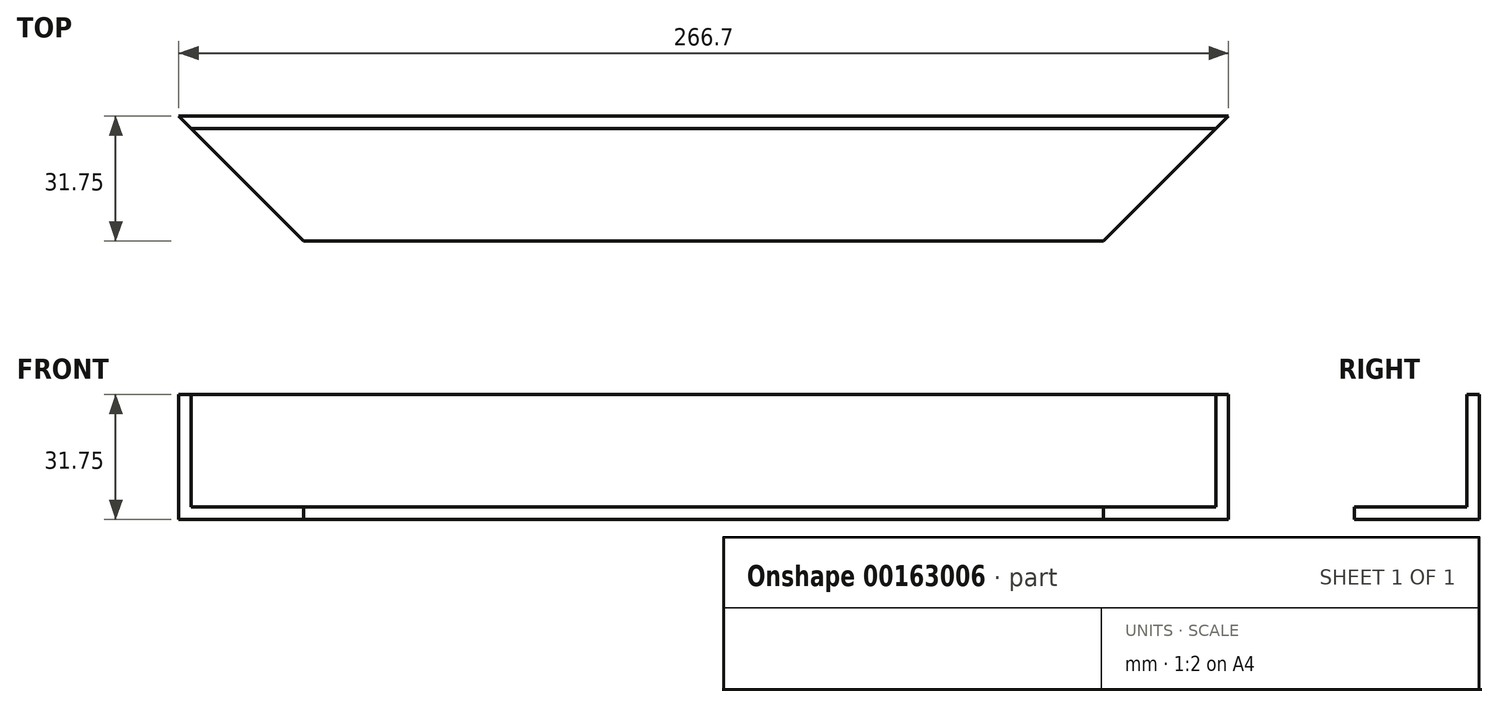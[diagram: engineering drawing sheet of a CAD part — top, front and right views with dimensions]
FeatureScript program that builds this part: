
annotation { "Feature Type Name" : "Feature", "Feature Type Description" : "" }
export const myFeature = defineFeature(function(context is Context, id is Id, definition is map)
    precondition{}
    {
        {
            var Q0;
            Q0=qCreatedBy(makeId("Right.planeOp"),FACE);
            var sketch = newSketch(context, id + "F0", { "sketchPlane" : qUnion([Q0])});
            skLineSegment(sketch, "E0", {"start": v(0, 0) * mm, "end": v(0, 31.75) * mm});
            skLineSegment(sketch, "E1", {"start": v(0, 0) * mm, "end": v(-31.75, 0) * mm});
            skLineSegment(sketch, "E2", {"start": v(-31.75, 0) * mm, "end": v(-31.75, 3.17) * mm});
            skLineSegment(sketch, "E3", {"start": v(-31.75, 3.17) * mm, "end": v(-3.17, 3.17) * mm});
            skLineSegment(sketch, "E4", {"start": v(-3.17, 3.17) * mm, "end": v(-3.17, 31.75) * mm});
            skLineSegment(sketch, "E5", {"start": v(-3.17, 31.75) * mm, "end": v(0, 31.75) * mm});
            skSolve(sketch);
        }
        {
            var Q0;
            Q0 = qSketchRegion(id + "F0", true);
            extrude(context, id + "F1", {"entities" : qUnion([Q0]), "depth" : 266.7 * mm});
        }
        {
            var Q0;
            Q0=qCreatedBy(makeId("Right.planeOp"),FACE);
            var Q1;
            Q1=makeQuery(id+"F1.opExtrude","CAP_EDGE",EDGE,{"disambiguationData":[OSD([sQuery(id+"F0.wireOp",EDGE,"E0")])],"isStart":true});
            cPlane(context, id + "F2", {"entities" : qUnion([Q0, Q1]), "cplaneType" : CPlaneType.LINE_ANGLE, "offset" : 25.4 * mm, "angle" : 45 * degree, "width" : 152.4 * mm, "height" : 152.4 * mm});
        }
        {
            var Q0;
            Q0=makeQuery(id+"F1.opExtrude","CAP_FACE",FACE,{"disambiguationData":[OSD([sQuery(id+"F0.wireOp",EDGE,"E0"),sQuery(id+"F0.wireOp",EDGE,"E1"),sQuery(id+"F0.wireOp",EDGE,"E2"),sQuery(id+"F0.wireOp",EDGE,"E3"),sQuery(id+"F0.wireOp",EDGE,"E4"),sQuery(id+"F0.wireOp",EDGE,"E5")])],"isStart":true});
            var Q1;
            Q1=qCreatedBy(id+"F2.planeOp",FACE);
            extrude(context, id + "F3", {"entities" : qUnion([Q0]), "operationType" : NewBodyOperationType.REMOVE, "endBound" : BoundingType.UP_TO_SURFACE, "oppositeDirection" : true, "endBoundEntityFace" : qUnion([Q1]), "depth" : 25.4 * mm});
        }
        {
            var Q0;
            Q0=makeQuery(id+"F1.opExtrude","CAP_EDGE",EDGE,{"disambiguationData":[OSD([sQuery(id+"F0.wireOp",EDGE,"E0")])],"isStart":false});
            cPlane(context, id + "F4", {"entities" : qUnion([Q0]), "cplaneType" : CPlaneType.LINE_ANGLE, "offset" : 25.4 * mm, "angle" : 315 * degree, "width" : 152.4 * mm, "height" : 152.4 * mm});
        }
        {
            var Q0;
            Q0=makeQuery(id+"F1.opExtrude","CAP_FACE",FACE,{"disambiguationData":[OSD([sQuery(id+"F0.wireOp",EDGE,"E0"),sQuery(id+"F0.wireOp",EDGE,"E1"),sQuery(id+"F0.wireOp",EDGE,"E2"),sQuery(id+"F0.wireOp",EDGE,"E3"),sQuery(id+"F0.wireOp",EDGE,"E4"),sQuery(id+"F0.wireOp",EDGE,"E5")])],"isStart":false});
            var Q1;
            Q1=qCreatedBy(id+"F4.planeOp",FACE);
            extrude(context, id + "F5", {"entities" : qUnion([Q0]), "operationType" : NewBodyOperationType.REMOVE, "endBound" : BoundingType.UP_TO_SURFACE, "oppositeDirection" : true, "endBoundEntityFace" : qUnion([Q1]), "depth" : 25.4 * mm});
        }
    });
